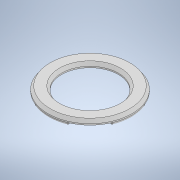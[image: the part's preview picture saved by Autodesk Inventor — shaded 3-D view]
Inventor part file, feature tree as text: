
AUTODESK INVENTOR PART (.ipt)
format: ipt  version: 2020 (Build 240168000, 168)  size: 203,776 bytes
history: native  units: mm
features: projected_geometry x4, revolve x3, sketch x3, chamfer x2, other x1, pattern_circular x1
ambient origin geometry x8: Origin, YZ Plane, XZ Plane, XY Plane, X Axis, Y Axis, Z Axis, Center Point
bodies: Body1 (feature_tree)
feature tree (14):
  other  "Твердое тело1"
  revolve  "Вращение1"
  chamfer  "Фаска1"  Distance=10.0mm
  revolve  "Вращение2"
  pattern_circular  "Круговой массив1"  [2 undecoded]
  revolve  "Вращение3"
  chamfer  "Фаска2"  Distance=2.0mm
  sketch  "Эскиз1"
  sketch  "Эскиз2"
  projected_geometry  "Спроецированная петля1"
  projected_geometry  "Спроецированная петля2"
  projected_geometry  "Спроецированная петля3"
  sketch  "Эскиз3"
  projected_geometry  "Спроецированная петля4"
note: 2 required parameter values undecoded (feature->parameter linkage not recoverable at this tier; creation-order binding heuristic only, values carry confidence <= 0.55)
